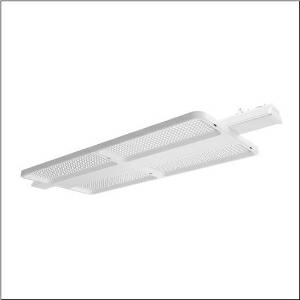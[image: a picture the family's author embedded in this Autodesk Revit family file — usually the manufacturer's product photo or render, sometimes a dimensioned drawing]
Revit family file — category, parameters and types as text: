
# Revit family: highbay_21_fur_licross_r__tragschiene_maxi_52hn11db4wla_13fd
name_source: partatom
category: Lighting Fixtures
units: mm (PartAtom-declared; Revit-internal decimal feet)

## family parameters
Cut with Voids When Loaded = No
Host = Face
Light Source = No
Part Type = Normal
Room Calculation Point = No
Round Connector Dimension = Use Diameter
Shared = No

## types (1)
- --- (1 x LED, 64000 lm, 345 W, 4000K)
    Apparent Load = 345 VA
    CIE Flux Codes = 89 97 99 100 100
    Color Rendering = 80
    Color Temperature = 4000K
    Default Elevation = 1800 mm
    Description = high bay luminaire Highbay 21 for Licross® trunking rail maxi; direct symmetric narrow distribution, light control with lens of PMMA; UGR ≤ 22 (X = 4H | Y = 8H | S = 0.25H | reflection values 70/50/20); luminous flux: 64.000lm; light colour: 840, colour temperature: 4000K, MacAdam ≤ 3 SDCM (initial), colour rendering: CRI > 80; luminous efficacy: 185,5lm/W; rated service life: 75.000h (L80/B50) at AT= ta max; control: DALI 2; luminaire connection: plug, 5-pole, with phase selectionmains connection: 230..240V, AC 50/60Hz; connected load: 345W; protection rating (complete): IP64; insulation class (complete): insulation class I (protective earthing); protection symbol: D; impact resistance: IK07; certification: CE, ENEC, VDE, UKCA; internal wiring halogen-free; luminaire corresponds to IFS (International Featured Standards) requirements for safety and quality in the food industry; LABS conformity tested according to VDMA 24364:2018-05; housing frame of high-performance plastic PA6, matt traffic white (RAL 9016); cover of PMMA; fixing on rail side of steel, galvanised, white; blank cover of PC/ABS, traffic white (RAL 9016); dimension (LxWxH): 1.250 x 442 x 71mm; permissible operating ambient temperature: -40..+50°C (reducing of maximum allowable ambient temperature of 5°C with ceiling mounting); packaging unit: 1 piece
    Height = 72 mm  [stored 0.23622 ft]
    Lamp = 1 x LED
    Lamp Light Flux = 64000 lm
    Lamp Power = 345 W
    Lamp count = 1
    Length = 946 mm
    Luminous efficacy = 186 lm/W
    Manufacturer = Siteco
    ModVariant = No
    Model = 52HN11DB4WLA
    Mounting Place = Ceiling
    Mounting Type = Pendant
    Number of Poles = 1
    OnlyDefault = Yes
    Power Factor = 1
    Product Name = Highbay 21 für Licross® Tragschiene maxi
    Product group = high bay luminaire
    ProductGroupID = 901
    Protection Class = Protection class I
    Protection Degree = IP 64
    RLX_Detail_Level = 1
    RLX_Emergency_Light_Flux = 0 lm
    RLX_Emergency_Type = 0
    RLX_Emergency_Type_DB = No
    RlxData = <blob elided: 130029 chars, md5=a0829c6a>
    Socket = socket
    Standby Power = 0 W
    System Light Flux = 64001 lm
    System Power = 345 W
    Type Comments = factory setting: luminous flux: 100 % | dim-lin: 254 | 792 mA
    Type Image = l_1361711.jpg
    URL = http://relux.com
    VarID = @adj_015205
    Voltage = 0 V
    Weight = 0.00 kg
    Width = 442 mm

note: [stored X ft] marks values corroborated as IEEE doubles in the binary element streams (Revit-internal decimal feet)

## geometry (parser evidence)
native form markers: Blend x4, Sweep x10
no freeform markers — native parametric forms only
